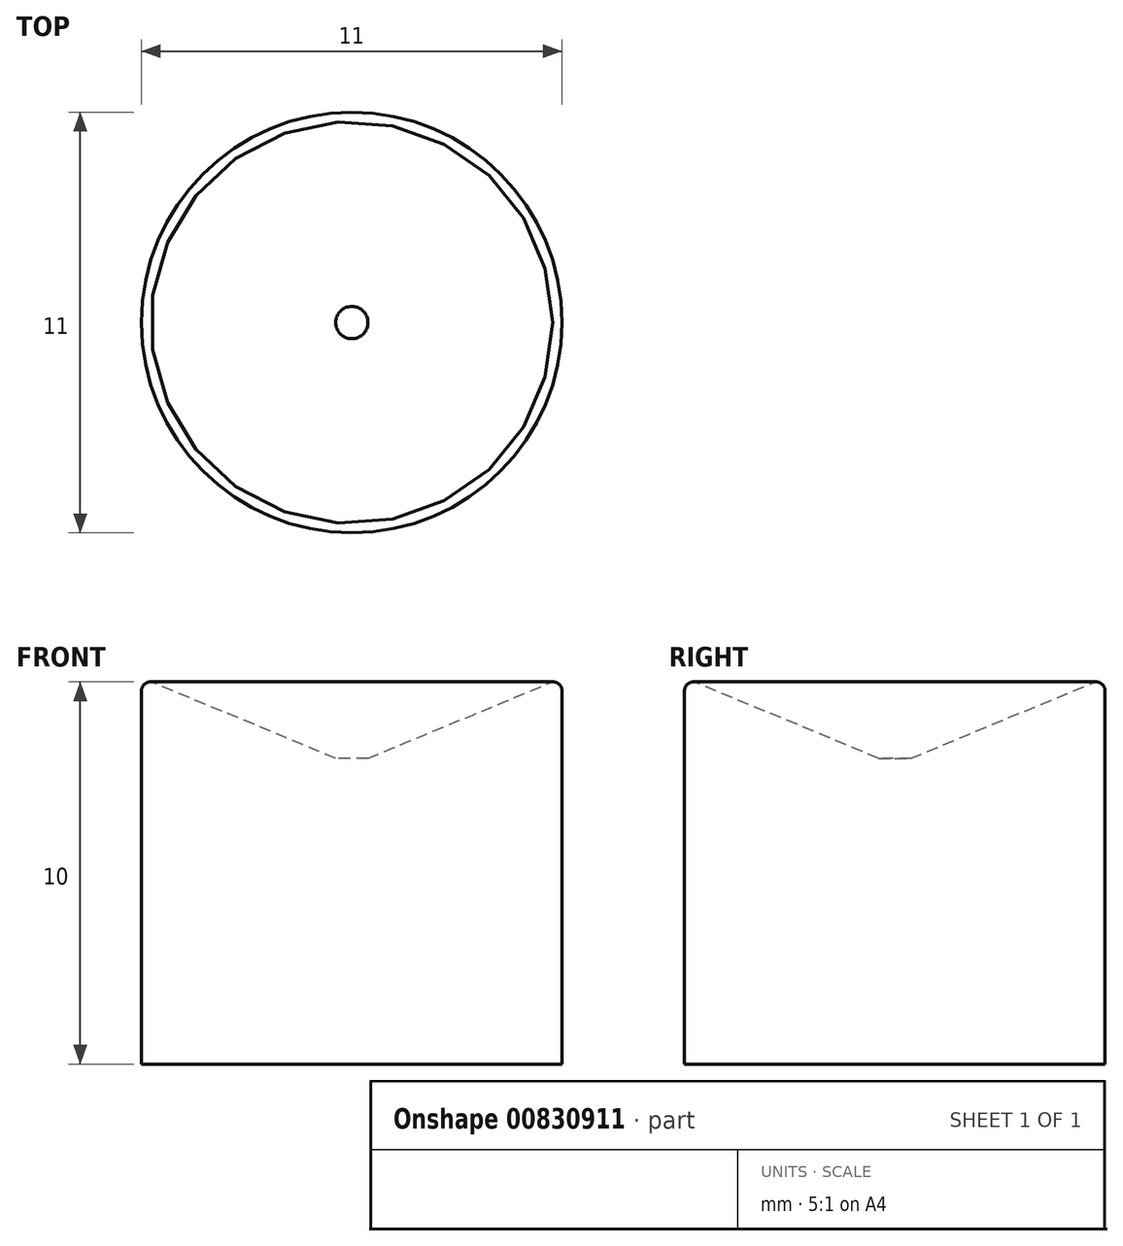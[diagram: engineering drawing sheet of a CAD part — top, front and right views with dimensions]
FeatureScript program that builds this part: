
annotation { "Feature Type Name" : "Feature", "Feature Type Description" : "" }
export const myFeature = defineFeature(function(context is Context, id is Id, definition is map)
    precondition{}
    {
        {
            var Q0;
            Q0=qCreatedBy(makeId("Top.planeOp"),FACE);
            var sketch = newSketch(context, id + "F0", { "sketchPlane" : qUnion([Q0])});
            skCircle(sketch, "E0", {"center": v(0, 0) * mm, "radius": 5.5 * mm});
            skSolve(sketch);
        }
        {
            var Q0;
            Q0=makeQuery(id+"F0.imprint","IMPRINT",FACE,{"disambiguationData":[TD([[makeQuery(id+"F0.imprint","IMPRINT",EDGE,{"derivedFrom":sQuery(id+"F0.wireOp",EDGE,"E0")}),1.0]])]});
            extrude(context, id + "F1", {"entities" : qUnion([Q0]), "depth" : 10 * mm, "offsetDistance" : 25 * mm});
        }
        {
            var Q0;
            Q0=makeQuery(id+"F1.opExtrude","CAP_FACE",FACE,{"disambiguationData":[OSD([sQuery(id+"F0.wireOp",EDGE,"E0")])],"isStart":false});
            fillet(context, id + "F2", {"entities" : qUnion([Q0]), "radius" : 0.24 * mm, "tangentPropagation" : true, "allowEdgeOverflow" : false});
        }
        {
            var Q0;
            Q0=makeQuery(id+"F1.opExtrude","CAP_FACE",FACE,{"disambiguationData":[OSD([sQuery(id+"F0.wireOp",EDGE,"E0")])],"isStart":false});
            var sketch = newSketch(context, id + "F3", { "sketchPlane" : qUnion([Q0])});
            skCircle(sketch, "E1", {"center": v(0, 0) * mm, "radius": 4.25 * mm});
            skSolve(sketch);
        }
        {
            var Q0;
            Q0=sQuery(id+"F3.wireOp",VERTEX,"E1.center");
            var Q1;
            Q1=makeQuery(id+"F1.opExtrude","SWEPT_BODY",BODY,{"disambiguationData":[OSD([sQuery(id+"F0.wireOp",EDGE,"E0")])]});
            hole(context, id + "F4", {"style" : HoleStyle.C_SINK, "endStyle" : HoleEndStyle.THROUGH, "holeDiameter" : 0.1 * mm, "cSinkDiameter" : 10.5 * mm, "cSinkAngle" : 135 * degree, "majorDiameter" : 5 * mm, "isTappedThrough" : true, "tappedDepth" : 12 * mm, "tapClearance" : 3, "locations" : qUnion([Q0]), "scope" : qUnion([Q1])});
        }
        {
            var Q0;
            Q0 = qSketchRegion(id + "F0", true);
            extrude(context, id + "F5", {"entities" : qUnion([Q0]), "operationType" : NewBodyOperationType.ADD, "depth" : 8 * mm, "offsetDistance" : 25 * mm});
        }
    });
